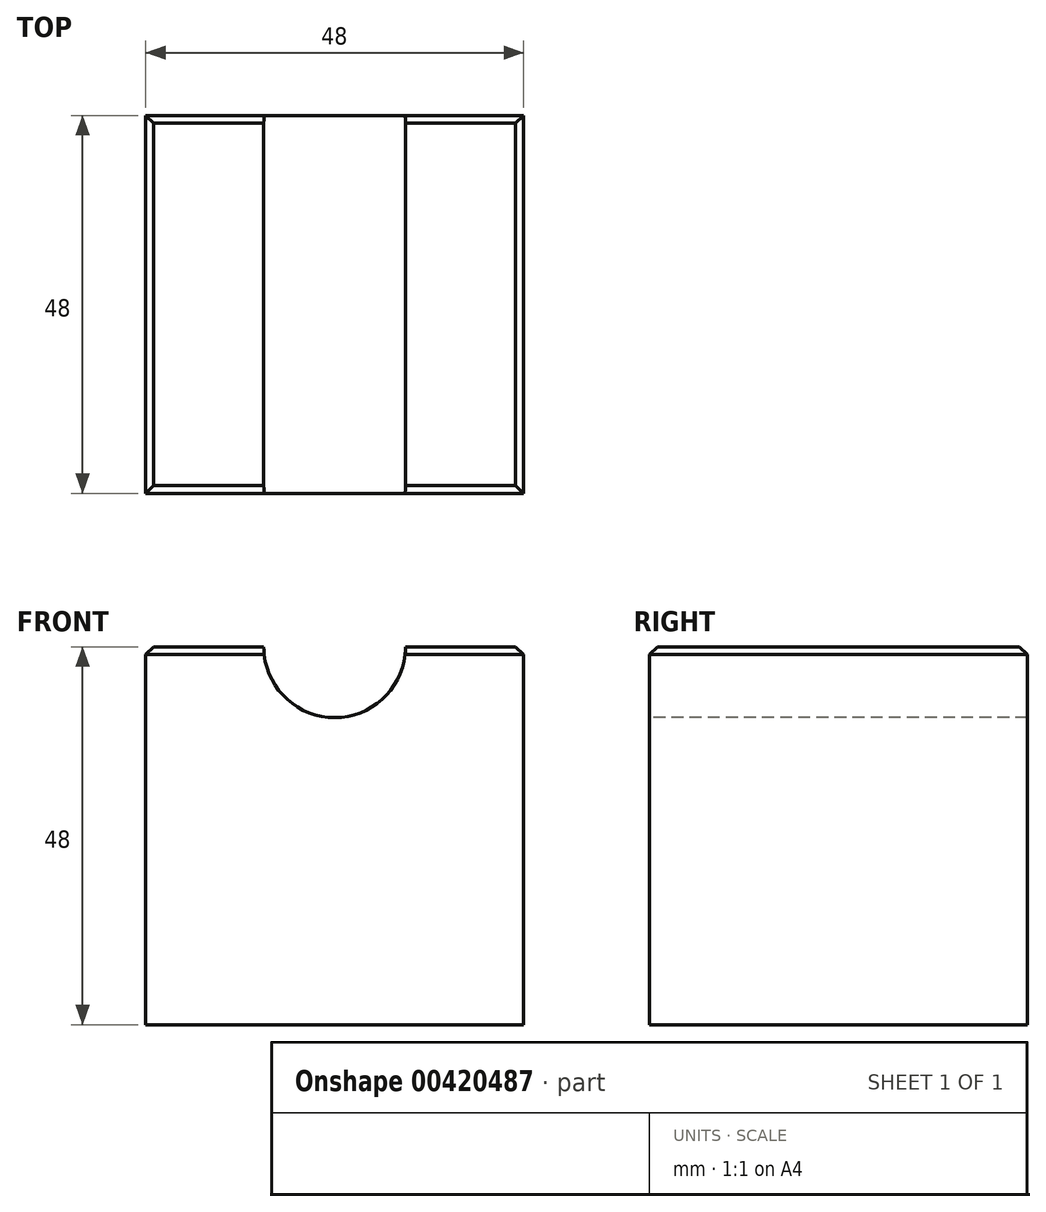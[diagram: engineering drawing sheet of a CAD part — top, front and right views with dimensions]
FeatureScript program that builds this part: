
annotation { "Feature Type Name" : "Feature", "Feature Type Description" : "" }
export const myFeature = defineFeature(function(context is Context, id is Id, definition is map)
    precondition{}
    {
        {
            var Q0;
            Q0=qCreatedBy(makeId("Front.planeOp"),FACE);
            var sketch = newSketch(context, id + "F0", { "sketchPlane" : qUnion([Q0])});
            skLineSegment(sketch, "E0.bottom", {"start": v(-24, 24) * mm, "end": v(24, 24) * mm});
            skLineSegment(sketch, "E0.top", {"start": v(-24, -24) * mm, "end": v(24, -24) * mm});
            skLineSegment(sketch, "E0.left", {"start": v(-24, 24) * mm, "end": v(-24, -24) * mm});
            skLineSegment(sketch, "E0.right", {"start": v(24, 24) * mm, "end": v(24, -24) * mm});
            skPoint(sketch, "E0.middle", {"position": v(0, 0) * mm});
            skSolve(sketch);
        }
        {
            var Q0;
            Q0=makeQuery(id+"F0.imprint","IMPRINT",FACE,{"disambiguationData":[TD([[makeQuery(id+"F0.imprint","IMPRINT",EDGE,{"derivedFrom":sQuery(id+"F0.wireOp",EDGE,"E0.bottom")}),-1.0]])]});
            extrude(context, id + "F1", {"entities" : qUnion([Q0]), "depth" : 48 * mm});
        }
        {
            var Q0;
            Q0=makeQuery(id+"F1.opExtrude","CAP_FACE",FACE,{"disambiguationData":[OSD([sQuery(id+"F0.wireOp",EDGE,"E0.bottom"),sQuery(id+"F0.wireOp",EDGE,"E0.top"),sQuery(id+"F0.wireOp",EDGE,"E0.left"),sQuery(id+"F0.wireOp",EDGE,"E0.right")])],"isStart":false});
            var sketch = newSketch(context, id + "F2", { "sketchPlane" : qUnion([Q0])});
            skCircle(sketch, "E1", {"center": v(0, 24) * mm, "radius": 9 * mm});
            skSolve(sketch);
        }
        {
            var Q0;
            {var subQ0=sQuery(id+"F2.wireOp",EDGE,"E1");var subQ1=makeQuery(id+"F1.opExtrude","CAP_EDGE",EDGE,{"disambiguationData":[OSD([sQuery(id+"F0.wireOp",EDGE,"E0.bottom")])],"isStart":false});var subQ2=makeQuery(id+"F2.imprint","INTERSECT",VERTEX,{"disambiguationData":[OD(0.0)],"derivedFrom":[subQ1,subQ0]});Q0=makeQuery(id+"F2.imprint","IMPRINT",FACE,{"disambiguationData":[TD([[makeQuery(id+"F2.imprint","IMPRINT",EDGE,{"disambiguationData":[TD([[subQ2,-1.0]])],"derivedFrom":subQ0}),1.0]])]});}
            extrude(context, id + "F3", {"entities" : qUnion([Q0]), "operationType" : NewBodyOperationType.REMOVE, "oppositeDirection" : true, "depth" : 48 * mm});
        }
        {
            var Q0;
            {var subQ0=sQuery(id+"F0.wireOp",EDGE,"E0.bottom");var subQ1=sQuery(id+"F0.wireOp",EDGE,"E0.right");Q0=makeQuery(id+"F3.boolean.opBoolean","SPLIT",EDGE,{"disambiguationData":[TD([makeQuery(id+"F1.opExtrude","SWEPT_FACE",FACE,{"disambiguationData":[OSD([subQ1])]})])],"derivedFrom":makeQuery(id+"F1.opExtrude","CAP_EDGE",EDGE,{"disambiguationData":[OSD([subQ0])],"isStart":false})});}
            var Q1;
            Q1=makeQuery(id+"F1.opExtrude","SWEPT_EDGE",EDGE,{"disambiguationData":[OSD([sQuery(id+"F0.wireOp",EDGE,"E0.bottom"),sQuery(id+"F0.wireOp",EDGE,"E0.right")])]});
            var Q2;
            {var subQ0=sQuery(id+"F0.wireOp",EDGE,"E0.bottom");var subQ1=sQuery(id+"F0.wireOp",EDGE,"E0.right");Q2=makeQuery(id+"F3.boolean.opBoolean","SPLIT",EDGE,{"disambiguationData":[TD([makeQuery(id+"F1.opExtrude","SWEPT_FACE",FACE,{"disambiguationData":[OSD([subQ1])]})])],"derivedFrom":makeQuery(id+"F1.opExtrude","CAP_EDGE",EDGE,{"disambiguationData":[OSD([subQ0])],"isStart":true})});}
            var Q3;
            {var subQ0=sQuery(id+"F0.wireOp",EDGE,"E0.bottom");var subQ1=sQuery(id+"F0.wireOp",EDGE,"E0.left");Q3=makeQuery(id+"F3.boolean.opBoolean","SPLIT",EDGE,{"disambiguationData":[TD([makeQuery(id+"F1.opExtrude","SWEPT_FACE",FACE,{"disambiguationData":[OSD([subQ1])]})])],"derivedFrom":makeQuery(id+"F1.opExtrude","CAP_EDGE",EDGE,{"disambiguationData":[OSD([subQ0])],"isStart":true})});}
            var Q4;
            Q4=makeQuery(id+"F1.opExtrude","SWEPT_EDGE",EDGE,{"disambiguationData":[OSD([sQuery(id+"F0.wireOp",EDGE,"E0.bottom"),sQuery(id+"F0.wireOp",EDGE,"E0.left")])]});
            var Q5;
            {var subQ0=sQuery(id+"F0.wireOp",EDGE,"E0.bottom");var subQ1=sQuery(id+"F0.wireOp",EDGE,"E0.left");Q5=makeQuery(id+"F3.boolean.opBoolean","SPLIT",EDGE,{"disambiguationData":[TD([makeQuery(id+"F1.opExtrude","SWEPT_FACE",FACE,{"disambiguationData":[OSD([subQ1])]})])],"derivedFrom":makeQuery(id+"F1.opExtrude","CAP_EDGE",EDGE,{"disambiguationData":[OSD([subQ0])],"isStart":false})});}
            chamfer(context, id + "F4", {"entities" : qUnion([Q0, Q1, Q2, Q3, Q4, Q5]), "width" : 1 * mm, "tangentPropagation" : true});
        }
    });
